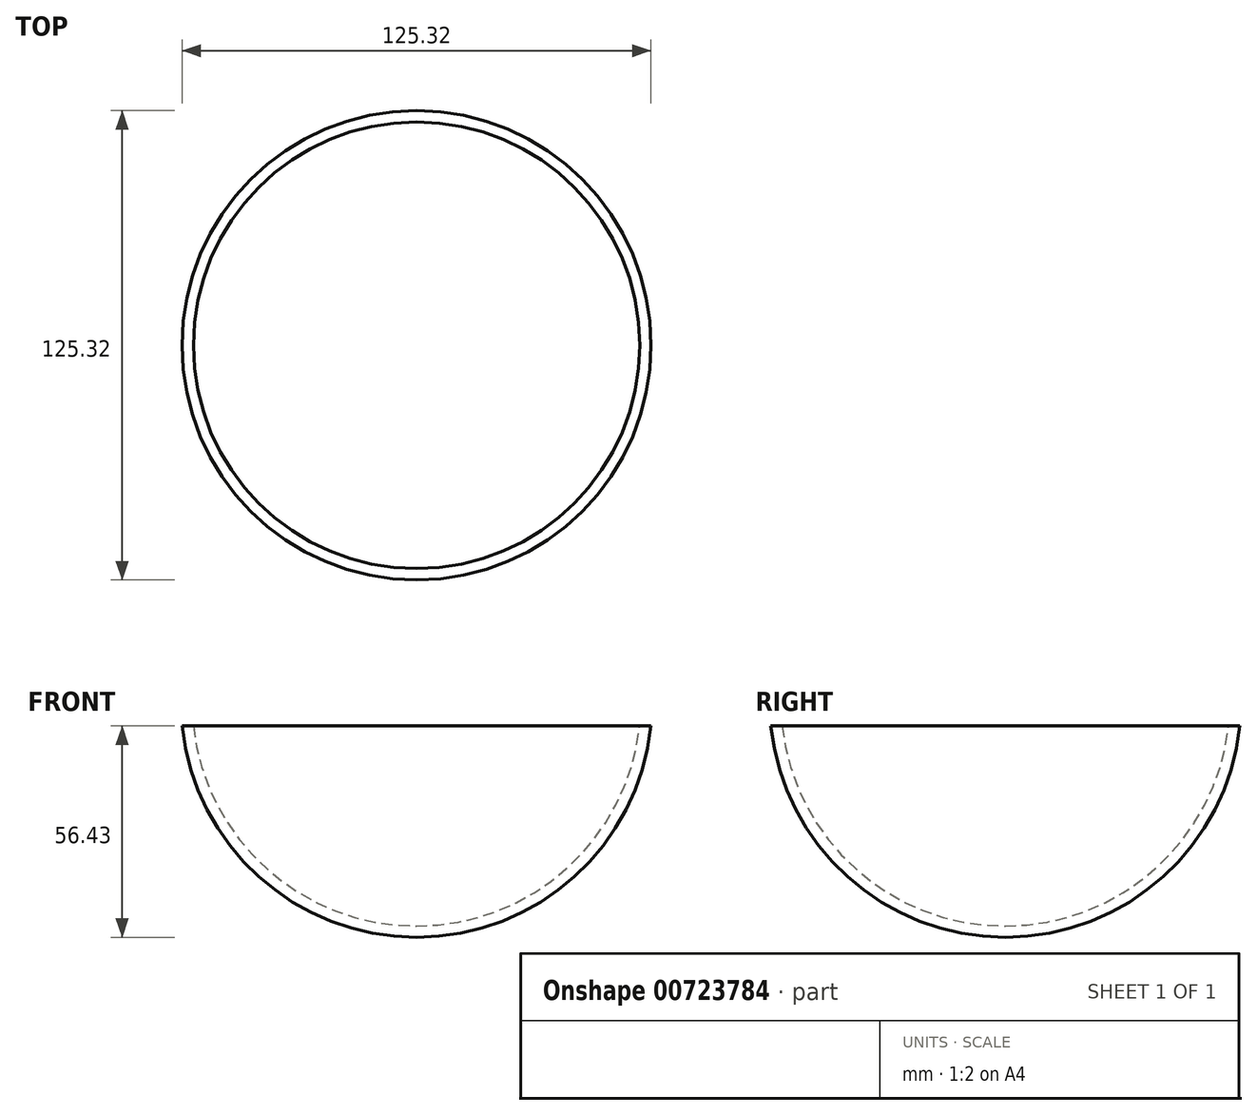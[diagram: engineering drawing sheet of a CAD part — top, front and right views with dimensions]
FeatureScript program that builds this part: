
annotation { "Feature Type Name" : "Feature", "Feature Type Description" : "" }
export const myFeature = defineFeature(function(context is Context, id is Id, definition is map)
    precondition{}
    {
        {
            var Q0;
            Q0=qCreatedBy(makeId("Top.planeOp"),FACE);
            var sketch = newSketch(context, id + "F0", { "sketchPlane" : qUnion([Q0])});
            skArc(sketch, "E0", {"start": v(-63, 0) * mm, "mid": v(0, -63) * mm, "end": v(63, 0) * mm});
            skArc(sketch, "E1.0", {"start": v(-60, 0) * mm, "mid": v(0, -60) * mm, "end": v(60, 0) * mm});
            skLineSegment(sketch, "E2", {"start": v(60, 0) * mm, "end": v(63, 0) * mm});
            skLineSegment(sketch, "E3", {"start": v(-60, 0) * mm, "end": v(-63, 0) * mm});
            skLineSegment(sketch, "E4", {"start": v(60, 0) * mm, "end": v(-60, 0) * mm, "construction": true});
            skSolve(sketch);
        }
        {
            var Q0;
            Q0=makeQuery(id+"F0.imprint","IMPRINT",FACE,{"disambiguationData":[TD([[makeQuery(id+"F0.imprint","IMPRINT",EDGE,{"derivedFrom":sQuery(id+"F0.wireOp",EDGE,"E0")}),1.0]])]});
            var Q1;
            Q1=sQuery(id+"F0.wireOp",EDGE,"E4");
            revolve(context, id + "F1", {"entities" : qUnion([Q0]), "axis" : qUnion([Q1]), "revolveType" : RevolveType.ONE_DIRECTION, "angle" : 360 * degree});
        }
        {
            var Q0;
            Q0=qCreatedBy(makeId("Right.planeOp"),FACE);
            var sketch = newSketch(context, id + "F2", { "sketchPlane" : qUnion([Q0])});
            skLineSegment(sketch, "E5.MirrorCS", {"start": v(75, 63.43) * mm, "end": v(75, 3.43) * mm});
            skLineSegment(sketch, "E6.MirrorCS", {"start": v(-75, 63.43) * mm, "end": v(75, 63.43) * mm});
            skLineSegment(sketch, "E7.MirrorCS", {"start": v(-75, 3.43) * mm, "end": v(-75, 63.43) * mm});
            skLineSegment(sketch, "E8", {"start": v(75, 3.43) * mm, "end": v(75, -6.57) * mm});
            skLineSegment(sketch, "E9", {"start": v(75, -6.57) * mm, "end": v(-75, -6.57) * mm});
            skLineSegment(sketch, "E10", {"start": v(-75, -6.57) * mm, "end": v(-75, 3.43) * mm});
            skSolve(sketch);
        }
        {
            var Q0;
            Q0=qSketchRegion(id+"F2",true);
            extrude(context, id + "F3", {"entities" : qUnion([Q0]), "operationType" : NewBodyOperationType.REMOVE, "oppositeDirection" : true, "depth" : 126 * mm, "symmetric" : true});
        }
    });
